# Revit family: Arboles UK - 900199CW - SS Pillar Bib Tap Special Water Fixed Nozzle
name_source: partatom
category: Plumbing Fixtures
revit_build: Autodesk Revit 2015 (Build: 20140606_1530(x64)
units: mm (PartAtom-declared; Revit-internal decimal feet)

## types (2) — shared parameters
Colour = White RAL 9016
Default Elevation = 1219 mm
Depth = 250mm
Pressure = 100PSI
Spare Handwheel = Pt No 960200
Standout = 150mm
Width = 50mm

## per-type parameters (varying)
| type | Base to nozzle | Description | Material | Overall height | Shank |
| 900120CW-WA | 200mm | Bench mounted pillar tap, cold water WRAS | Brass with Rilsan plastic coated | 280mm | 1/2" BSP x 60mm Long flat ended |
| 900199DW-W | 240mm | Bench mounted pillar tap, Special water | Stainless Steel, 316 & 304 with Rilsan plastic coating | 340mm | 3/8" BSP x 60mm Long flat ended |

note: column(s) folded — value = type name in every type: Model

## geometry (parser evidence)
native form markers: Sweep x43
no freeform markers — native parametric forms only
